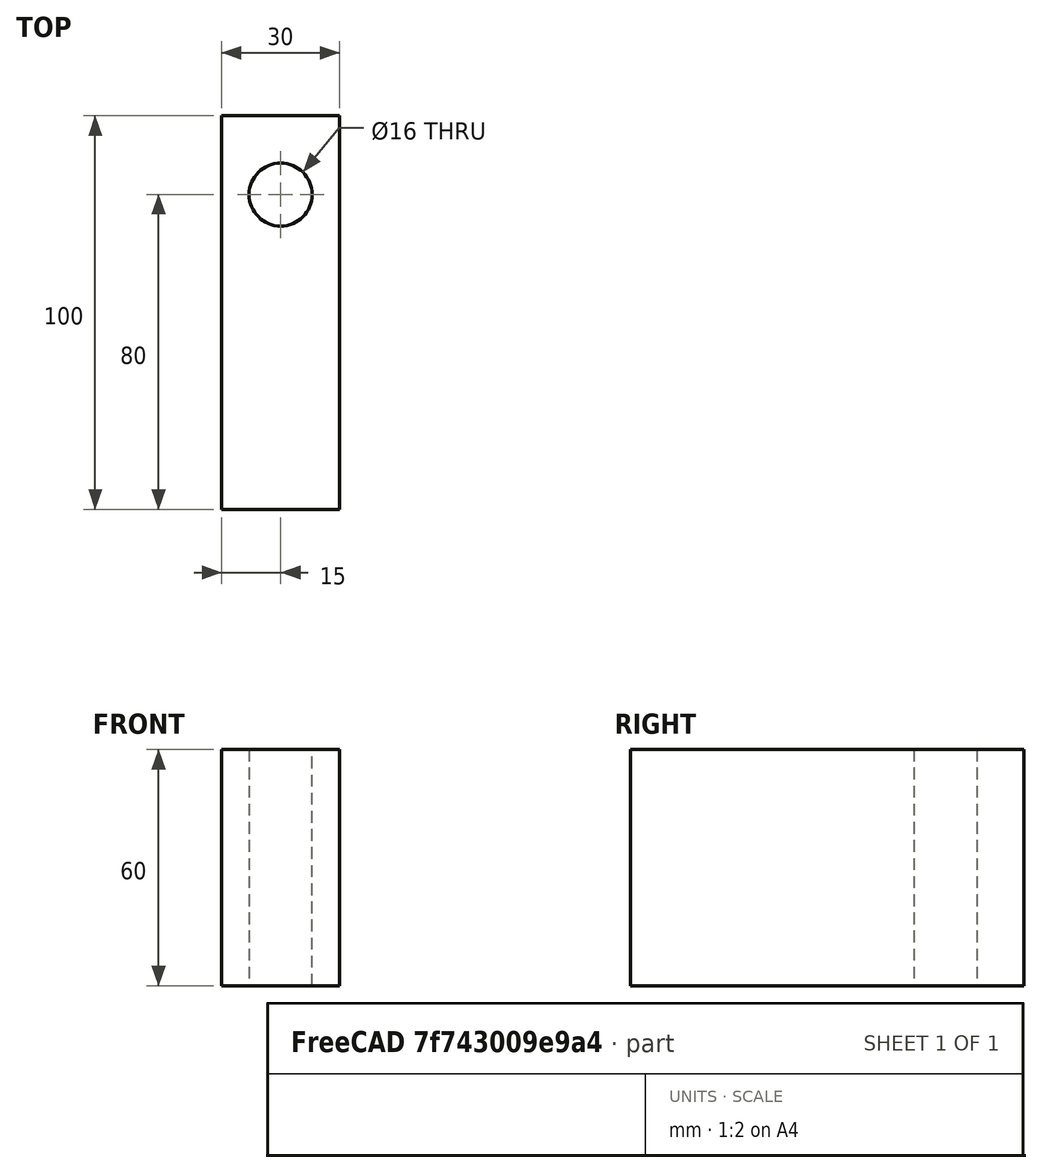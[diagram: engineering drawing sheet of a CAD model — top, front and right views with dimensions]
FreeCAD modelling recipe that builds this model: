
FCSTD DOCUMENT  (FreeCAD 0.19R24276 (Git))
Label: Opora_3
License: All rights reserved
LicenseURL: http://en.wikipedia.org/wiki/All_rights_reserved
objects: Sketcher::SketchObject×1, PartDesign::Pad×1, PartDesign::Body×1
note: 4 computed .brp shape members not serialized (recipe doc carries the construction recipe); baked Part::Feature solids carry a one-line shape summary decoded from their .brp

FEATURE [Sketcher::SketchObject] Sketch
  FullyConstrained = false
  MapMode = 5
  Support = -> [XY_Plane]
  sketch-geometry (5):
    g0: LineSegment StartX=0 StartY=0 StartZ=0 EndX=30 EndY=0 EndZ=0
    g1: LineSegment StartX=30 StartY=0 StartZ=0 EndX=30 EndY=100 EndZ=0
    g2: LineSegment StartX=30 StartY=100 StartZ=0 EndX=0 EndY=100 EndZ=0
    g3: LineSegment StartX=0 StartY=100 StartZ=0 EndX=0 EndY=0 EndZ=0
    g4: Circle CenterX=15 CenterY=80 CenterZ=0 NormalX=0 NormalY=0 NormalZ=1 AngleXU=0 Radius=8
  constraints (10):
    c: Coincident(g0,g1)
    c: Coincident(g1,g2)
    c: Coincident(g2,g3)
    c: Horizontal(g0)
    c: Horizontal(g2)
    c: Vertical(g1)
    c: Vertical(g3)
    c: DistanceY(g1,g1) = 100
    c: Distance(g0) = 30
    c: Diameter(g4) = 16
FEATURE [PartDesign::Pad] Pad
  Direction = (1,1,1)
  Length = 60
  Length2 = 100
  Profile = -> Sketch
  Type = 0
FEATURE [PartDesign::Body] Body
  Group = -> [Sketch,Pad]
  Origin = -> Origin
  Tip = -> Pad
